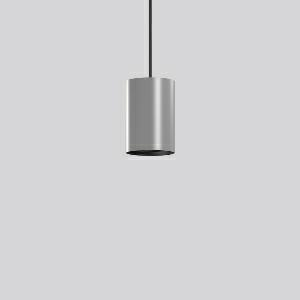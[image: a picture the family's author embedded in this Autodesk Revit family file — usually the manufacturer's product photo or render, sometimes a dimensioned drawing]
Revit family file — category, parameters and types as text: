
# Revit family: deecos_p_maxi_911534_004_1_ba5f
name_source: partatom
category: Lighting Fixtures
units: mm (PartAtom-declared; Revit-internal decimal feet)

## family parameters
Cut with Voids When Loaded = No
Host = Face
Light Source = No
Part Type = Normal
Room Calculation Point = No
Round Connector Dimension = Use Diameter
Shared = No

## types (1)
- DEECOS P maxi (1 x LED Modul 940, 2850 lm, 4000)
    Apparent Load = 25 VA
    Approval mark = CE
    CIE Flux Codes = 96 100 100 100 100
    Color Rendering = 92
    Color Temperature = 4000
    Default Elevation = 1800 mm
    Description = Series: DEECOS P maxi
Cylindrical pendant luminaire. Housing: die-cast aluminium, powder-coated. Canopy made of powder-coated sheet steel with magnetic attachment. Optical assembly with lens made of plastic (polycarbonate) for the best homogeneous light distribution - can be changed without tools. Best colour rendering index Ra>90. Transparent suspension cable 2 m, can be shortened. High quality converter without flickering and stroboscopic effect. The following accessories can be mounted without use of tools: interchangeable lenses, honeycomb louvre, clear and frosted diffusers, white interchangeable plastic ring. Decorative recessed suspension set available as accessory. 
Colour: silver
Diameter: 123 mm
Height: 181 mm
Suspension length: 2000 mm
Lamp: LED
Socket: without socket
Colour temperature: 4000K
Colour rendering index (CRI): 92
System power: 25 W
Rated luminous flux: 2850 lm
Luminous efficiency: 114 lm/W
Control gear: Regulated power supply
Protection class: I
Type of protection: IP 20
    Height = 181 mm
    Lamp = 1 x LED Modul 940
    Lamp Light Flux = 2850 lm
    Lamp count = 1
    Length = 123 mm
    Lifetime = 50000 h
    Luminous efficacy = 114 lm/W
    Manufacturer = RZB
    ModVariant = No
    Model = 911534.004.1
    Mounting Place = Ceiling
    Mounting Type = Pendant
    Number of Poles = 1
    OnlyDefault = Yes
    Power Factor = 1
    Product Name = DEECOS P maxi
    Product group = Pendant luminaires
    ProductGroupID = 902
    Protection Class = Protection class I
    Protection Degree = IP 20
    RLX_Detail_Level = 1
    RLX_Emergency_Light_Flux = 0 lm
    RLX_Emergency_Type = 0
    RLX_Emergency_Type_DB = No
    RlxData = <blob elided: 35709 chars, md5=90a72245>
    Socket = socket
    Standby Power = 0 W
    System Light Flux = 2850 lm
    System Power = 25 W
    Type Comments = Product without accessories
    Type Image = 911480.004.jpg
    URL = http://relux.com
    VarID = ---
    Voltage = 230 V
    Voltage Range = 220-240 V
    Weight = 0.00 kg
    Width = 0 mm  [stored 0 ft]

note: [stored X ft] marks values corroborated as IEEE doubles in the binary element streams (Revit-internal decimal feet)

## geometry (parser evidence)
native form markers: Blend x4, Sweep x9
no freeform markers — native parametric forms only
